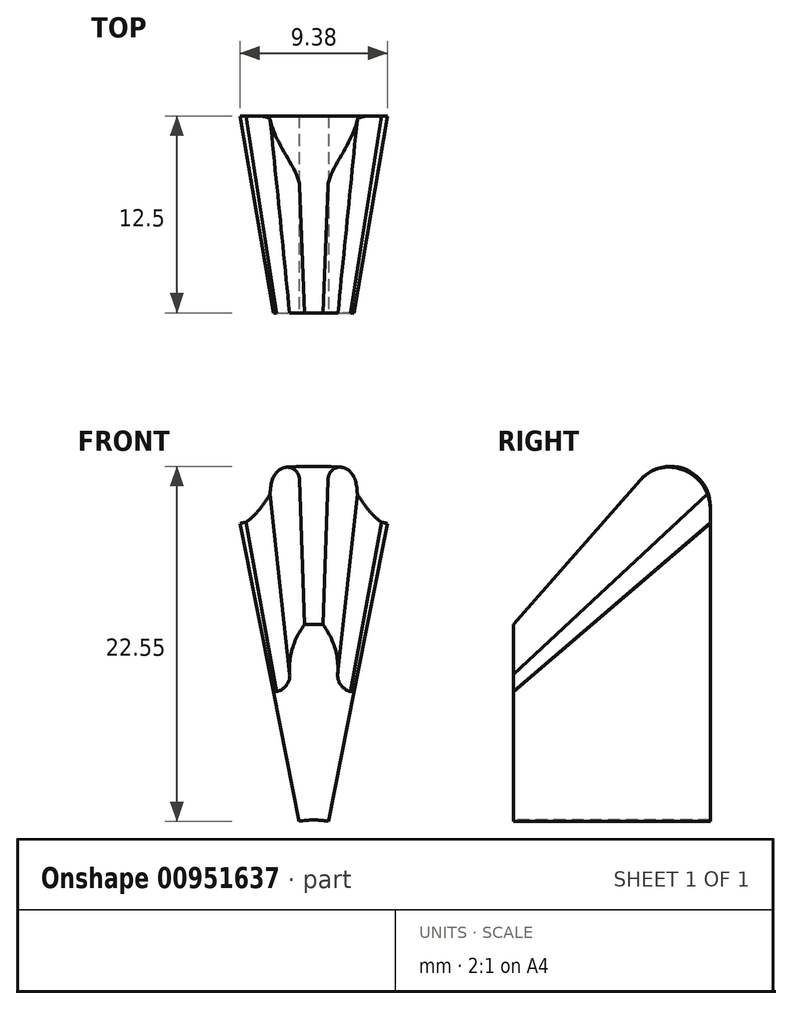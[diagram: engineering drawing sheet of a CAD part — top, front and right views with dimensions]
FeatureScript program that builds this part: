
annotation { "Feature Type Name" : "Feature", "Feature Type Description" : "" }
export const myFeature = defineFeature(function(context is Context, id is Id, definition is map)
    precondition{}
    {
        {
            var Q0;
            Q0=qCreatedBy(makeId("Front.planeOp"),FACE);
            cPlane(context, id + "F0", {"entities" : qUnion([Q0]), "cplaneType" : CPlaneType.OFFSET, "offset" : 12.7 * mm, "oppositeDirection" : true, "width" : 152.4 * mm, "height" : 152.4 * mm});
        }
        {
            assignVariable(context, id + "F1", {"name" : "GearThickness", "anyValue" : .1});
        }
        {
            var Q0;
            Q0=qCreatedBy(makeId("Front.planeOp"),FACE);
            var sketch = newSketch(context, id + "F2", { "sketchPlane" : qUnion([Q0])});
            skCircle(sketch, "E0", {"center": v(0, 0) * mm, "radius": 13 * mm});
            skSolve(sketch);
        }
        {
            var Q0;
            Q0=qSketchRegion(id+"F2",true);
            extrude(context, id + "F3", {"entities" : qUnion([Q0]), "endBound" : BoundingType.SYMMETRIC, "offsetDistance" : 25 * mm, "depth" : (getVariable(context, 'GearThickness')) * mm});
        }
        {
            var Q0;
            Q0=qCreatedBy(makeId("Front.planeOp"),FACE);
            var sketch = newSketch(context, id + "F4", { "sketchPlane" : qUnion([Q0])});
            skCircle(sketch, "E1", {"center": v(0, 0) * mm, "radius": 15 * mm, "construction": true});
            skLineSegment(sketch, "E2", {"start": v(0, 28.09) * mm, "end": v(0, 0) * mm, "construction": true});
            skLineSegment(sketch, "E3", {"start": v(0, 0) * mm, "end": v(-1.47, 14.93) * mm, "construction": true});
            skLineSegment(sketch, "E4", {"start": v(0, 0) * mm, "end": v(1.47, 14.93) * mm, "construction": true});
            skCircle(sketch, "E5", {"center": v(0, 0) * mm, "radius": 17 * mm, "construction": true});
            skArc(sketch, "E6", {"start": v(1.33, 12.93) * mm, "mid": v(0, 13) * mm, "end": v(-1.33, 12.93) * mm});
            skArc(sketch, "E7", {"start": v(0.58, 17) * mm, "mid": v(0, 17) * mm, "end": v(-0.58, 17) * mm});
            skLineSegment(sketch, "E8", {"start": v(-1.47, 14.93) * mm, "end": v(-1, 17.93) * mm, "construction": true});
            skLineSegment(sketch, "E9", {"start": v(-1.47, 14.93) * mm, "end": v(-0.58, 17) * mm, "construction": true});
            skArc(sketch, "E10", {"start": v(-0.58, 17) * mm, "mid": v(-1.45, 15.05) * mm, "end": v(-1.33, 12.93) * mm});
            skArc(sketch, "E11", {"start": v(1.33, 12.93) * mm, "mid": v(1.45, 15.05) * mm, "end": v(0.58, 17) * mm});
            skSolve(sketch);
        }
        {
            var Q0;
            Q0=qSketchRegion(id+"F4",true);
            extrude(context, id + "F5", {"entities" : qUnion([Q0]), "endBound" : BoundingType.SYMMETRIC, "depth" : (getVariable(context, 'GearThickness')) * mm});
        }
        {
            var Q0;
            Q0=qCreatedBy(makeId("Front.planeOp"),FACE);
            var sketch = newSketch(context, id + "F6", { "sketchPlane" : qUnion([Q0])});
            skArc(sketch, "E12", {"start": v(1.5, 13.86) * mm, "mid": v(1.7, 13.17) * mm, "end": v(2.32, 12.8) * mm});
            skArc(sketch, "E13", {"start": v(-2.32, 12.8) * mm, "mid": v(-1.7, 13.17) * mm, "end": v(-1.5, 13.86) * mm});
            skArc(sketch, "E14", {"start": v(2.32, 12.8) * mm, "mid": v(0, 13) * mm, "end": v(-2.32, 12.8) * mm});
            skLineSegment(sketch, "E15", {"start": v(-1.5, 13.86) * mm, "end": v(1.5, 13.86) * mm});
            skSolve(sketch);
        }
        {
            var Q0;
            Q0=qSketchRegion(id+"F6",true);
            extrude(context, id + "F7", {"entities" : qUnion([Q0]), "operationType" : NewBodyOperationType.ADD, "endBound" : BoundingType.SYMMETRIC, "offsetDistance" : 25.4 * mm, "depth" : (getVariable(context, 'GearThickness')) * mm});
        }
        {
            var Q0;
            Q0=makeQuery(id+"F3.opExtrude","CAP_FACE",FACE,{"disambiguationData":[OSD([sQuery(id+"F2.wireOp",EDGE,"E0")])],"isStart":true});
            var sketch = newSketch(context, id + "F8", { "sketchPlane" : qUnion([Q0])});
            skLineSegment(sketch, "E16", {"start": v(0, 0) * mm, "end": v(-2.32, 12.8) * mm, "construction": true});
            skLineSegment(sketch, "E17", {"start": v(0, 0) * mm, "end": v(-1.5, 13.86) * mm, "construction": true});
            skLineSegment(sketch, "E18", {"start": v(0, 0) * mm, "end": v(-0.58, 17) * mm, "construction": true});
            skLineSegment(sketch, "E19", {"start": v(0, 0) * mm, "end": v(0.58, 17) * mm, "construction": true});
            skLineSegment(sketch, "E20", {"start": v(0, 0) * mm, "end": v(1.5, 13.86) * mm, "construction": true});
            skLineSegment(sketch, "E21", {"start": v(0, 0) * mm, "end": v(2.32, 12.8) * mm, "construction": true});
            skSolve(sketch);
        }
        {
            var Q0;
            Q0=qCreatedBy(makeId("Top.planeOp"),FACE);
            var sketch = newSketch(context, id + "F9", { "sketchPlane" : qUnion([Q0])});
            skLineSegment(sketch, "E22", {"start": v(0, 0) * mm, "end": v(0, 9.45) * mm});
            skSolve(sketch);
        }
        {
            var Q0;
            Q0=sQuery(id+"F9.wireOp",VERTEX,"E22.end");
            var Q1;
            Q1=sQuery(id+"F9.wireOp",VERTEX,"E22.start");
            var Q2;
            Q2=sQuery(id+"F8.wireOp",VERTEX,"E16.end");
            cPlane(context, id + "F10", {"entities" : qUnion([Q0, Q1, Q2]), "cplaneType" : CPlaneType.THREE_POINT, "offset" : 25.4 * mm, "width" : 152.4 * mm, "height" : 152.4 * mm});
        }
        {
            var Q0;
            Q0=qCreatedBy(id+"F10.planeOp",FACE);
            var sketch = newSketch(context, id + "F11", { "sketchPlane" : qUnion([Q0])});
            skLineSegment(sketch, "E23", {"start": v(0.05, 13) * mm, "end": v(12.7, 25.65) * mm});
            skSolve(sketch);
        }
        {
            var Q0;
            Q0=sQuery(id+"F8.wireOp",VERTEX,"E20.start");
            var Q1;
            Q1=sQuery(id+"F9.wireOp",VERTEX,"E22.end");
            var Q2;
            Q2=sQuery(id+"F8.wireOp",VERTEX,"E17.end");
            cPlane(context, id + "F12", {"entities" : qUnion([Q0, Q1, Q2]), "cplaneType" : CPlaneType.THREE_POINT, "offset" : 25.4 * mm, "width" : 152.4 * mm, "height" : 152.4 * mm});
        }
        {
            var Q0;
            Q0=qCreatedBy(id+"F12.planeOp",FACE);
            var sketch = newSketch(context, id + "F13", { "sketchPlane" : qUnion([Q0])});
            skLineSegment(sketch, "E24", {"start": v(-0.05, 13.94) * mm, "end": v(-12.7, 26.6) * mm});
            skSolve(sketch);
        }
        {
            var Q0;
            Q0=sQuery(id+"F8.wireOp",VERTEX,"E18.end");
            var Q1;
            Q1=sQuery(id+"F9.wireOp",VERTEX,"E22.end");
            var Q2;
            Q2=sQuery(id+"F9.wireOp",VERTEX,"E22.start");
            cPlane(context, id + "F14", {"entities" : qUnion([Q0, Q1, Q2]), "cplaneType" : CPlaneType.THREE_POINT, "offset" : 25.4 * mm, "width" : 152.4 * mm, "height" : 152.4 * mm});
        }
        {
            var Q0;
            Q0=qCreatedBy(id+"F14.planeOp",FACE);
            var sketch = newSketch(context, id + "F15", { "sketchPlane" : qUnion([Q0])});
            skLineSegment(sketch, "E25", {"start": v(0.05, 17) * mm, "end": v(12.7, 29.65) * mm});
            skSolve(sketch);
        }
        {
            var Q0;
            Q0=sQuery(id+"F8.wireOp",VERTEX,"E20.start");
            var Q1;
            Q1=sQuery(id+"F8.wireOp",VERTEX,"E19.end");
            var Q2;
            Q2=sQuery(id+"F9.wireOp",VERTEX,"E22.end");
            cPlane(context, id + "F16", {"entities" : qUnion([Q0, Q1, Q2]), "cplaneType" : CPlaneType.THREE_POINT, "offset" : 25.4 * mm, "width" : 152.4 * mm, "height" : 152.4 * mm});
        }
        {
            var Q0;
            Q0=qCreatedBy(id+"F16.planeOp",FACE);
            var sketch = newSketch(context, id + "F17", { "sketchPlane" : qUnion([Q0])});
            skLineSegment(sketch, "E26", {"start": v(0.05, 17) * mm, "end": v(12.7, 29.65) * mm});
            skSolve(sketch);
        }
        {
            var Q0;
            Q0=sQuery(id+"F9.wireOp",VERTEX,"E22.end");
            var Q1;
            Q1=sQuery(id+"F9.wireOp",VERTEX,"E22.start");
            var Q2;
            Q2=sQuery(id+"F8.wireOp",VERTEX,"E20.end");
            cPlane(context, id + "F18", {"entities" : qUnion([Q0, Q1, Q2]), "cplaneType" : CPlaneType.THREE_POINT, "offset" : 25.4 * mm, "width" : 152.4 * mm, "height" : 152.4 * mm});
        }
        {
            var Q0;
            Q0=qCreatedBy(id+"F18.planeOp",FACE);
            var sketch = newSketch(context, id + "F19", { "sketchPlane" : qUnion([Q0])});
            skLineSegment(sketch, "E27", {"start": v(0.05, 13.94) * mm, "end": v(12.7, 26.6) * mm});
            skSolve(sketch);
        }
        {
            var Q0;
            Q0=sQuery(id+"F9.wireOp",VERTEX,"E22.end");
            var Q1;
            Q1=sQuery(id+"F8.wireOp",VERTEX,"E21.end");
            var Q2;
            Q2=sQuery(id+"F9.wireOp",VERTEX,"E22.start");
            cPlane(context, id + "F20", {"entities" : qUnion([Q0, Q1, Q2]), "cplaneType" : CPlaneType.THREE_POINT, "offset" : 25.4 * mm, "width" : 152.4 * mm, "height" : 152.4 * mm});
        }
        {
            var Q0;
            Q0=qCreatedBy(id+"F20.planeOp",FACE);
            var sketch = newSketch(context, id + "F21", { "sketchPlane" : qUnion([Q0])});
            skLineSegment(sketch, "E28", {"start": v(-0.05, 13) * mm, "end": v(-12.7, 25.65) * mm});
            skSolve(sketch);
        }
        {
            var Q0;
            Q0=qCreatedBy(id+"F0.planeOp",FACE);
            var sketch = newSketch(context, id + "F22", { "sketchPlane" : qUnion([Q0])});
            skArc(sketch, "E29", {"start": v(1.07, 31.42) * mm, "mid": v(0, 31.44) * mm, "end": v(-1.07, 31.42) * mm});
            skArc(sketch, "E30", {"start": v(-1.07, 31.42) * mm, "mid": v(-2.37, 28.66) * mm, "end": v(-2.79, 25.65) * mm});
            skArc(sketch, "E31", {"start": v(2.79, 25.65) * mm, "mid": v(2.37, 28.66) * mm, "end": v(1.07, 31.42) * mm});
            skArc(sketch, "E32", {"start": v(-4.3, 23.67) * mm, "mid": v(-3.4, 24.55) * mm, "end": v(-2.79, 25.65) * mm});
            skArc(sketch, "E33", {"start": v(2.79, 25.65) * mm, "mid": v(3.4, 24.55) * mm, "end": v(4.3, 23.67) * mm});
            skLineSegment(sketch, "E34", {"start": v(0, 0) * mm, "end": v(-4.3, 23.67) * mm, "construction": true});
            skLineSegment(sketch, "E35", {"start": v(0, 0) * mm, "end": v(-2.79, 25.65) * mm, "construction": true});
            skLineSegment(sketch, "E36", {"start": v(0, 0) * mm, "end": v(-1.07, 31.42) * mm, "construction": true});
            skLineSegment(sketch, "E37", {"start": v(0, 0) * mm, "end": v(1.07, 31.42) * mm, "construction": true});
            skLineSegment(sketch, "E38", {"start": v(0, 0) * mm, "end": v(2.79, 25.65) * mm, "construction": true});
            skLineSegment(sketch, "E39", {"start": v(0, 0) * mm, "end": v(4.3, 23.67) * mm, "construction": true});
            skLineSegment(sketch, "E40", {"start": v(0, 0) * mm, "end": v(4.7, 23.6) * mm});
            skLineSegment(sketch, "E41", {"start": v(0, 0) * mm, "end": v(-4.7, 23.6) * mm});
            skLineSegment(sketch, "E42", {"start": v(0, 0) * mm, "end": v(0, 20.32) * mm, "construction": true});
            skArc(sketch, "E43", {"start": v(-4.3, 23.67) * mm, "mid": v(-4.5, 23.63) * mm, "end": v(-4.7, 23.6) * mm});
            skArc(sketch, "E44", {"start": v(4.7, 23.6) * mm, "mid": v(4.5, 23.63) * mm, "end": v(4.3, 23.67) * mm});
            skSolve(sketch);
        }
        {
            var Q0;
            Q0=makeQuery(id+"F8.imprint","IMPRINT",FACE,{"disambiguationData":[TD([[makeQuery(id+"F8.imprint","IMPRINT",EDGE,{"derivedFrom":makeQuery(id+"F3.opExtrude","CAP_EDGE",EDGE,{"disambiguationData":[OSD([sQuery(id+"F2.wireOp",EDGE,"E0")])],"isStart":true})}),-1.0]])]});
            var sketch = newSketch(context, id + "F23", { "sketchPlane" : qUnion([Q0])});
            skLineSegment(sketch, "E45", {"start": v(0, 0) * mm, "end": v(-2.32, 12.8) * mm, "construction": true});
            skLineSegment(sketch, "E46", {"start": v(0, 0) * mm, "end": v(2.32, 12.8) * mm, "construction": true});
            skArc(sketch, "E47.0", {"start": v(-1.5, 13.86) * mm, "mid": v(-1.7, 13.17) * mm, "end": v(-2.32, 12.8) * mm});
            skArc(sketch, "E47.1", {"start": v(2.32, 12.8) * mm, "mid": v(1.7, 13.17) * mm, "end": v(1.5, 13.86) * mm});
            skArc(sketch, "E47.2", {"start": v(0.58, 17) * mm, "mid": v(1.34, 15.51) * mm, "end": v(1.5, 13.86) * mm});
            skArc(sketch, "E47.3", {"start": v(-0.58, 17) * mm, "mid": v(0, 17) * mm, "end": v(0.58, 17) * mm});
            skArc(sketch, "E47.4", {"start": v(-1.5, 13.86) * mm, "mid": v(-1.34, 15.51) * mm, "end": v(-0.58, 17) * mm});
            skLineSegment(sketch, "E48", {"start": v(0, 0) * mm, "end": v(-2.54, 12.75) * mm});
            skLineSegment(sketch, "E49", {"start": v(0, 0) * mm, "end": v(2.54, 12.75) * mm});
            skLineSegment(sketch, "E50", {"start": v(0, 0) * mm, "end": v(0, 6.32) * mm});
            skArc(sketch, "E51", {"start": v(-2.32, 12.8) * mm, "mid": v(-2.43, 12.77) * mm, "end": v(-2.54, 12.75) * mm});
            skArc(sketch, "E52", {"start": v(2.54, 12.75) * mm, "mid": v(2.43, 12.77) * mm, "end": v(2.32, 12.8) * mm});
            skSolve(sketch);
        }
        {
            var Q0;
            Q0 = qSketchRegion(id + "F22", true);
            var Q1;
            Q1 = qSketchRegion(id + "F23", true);
            var Q2;
            Q2=sQuery(id+"F23.wireOp",VERTEX,"E45.start");
            var Q3;
            Q3=sQuery(id+"F22.wireOp",VERTEX,"E34.start");
            var Q4;
            Q4=sQuery(id+"F23.wireOp",VERTEX,"E49.end");
            var Q5;
            Q5=sQuery(id+"F22.wireOp",VERTEX,"E41.end");
            var Q6;
            Q6=sQuery(id+"F23.wireOp",VERTEX,"E46.end");
            var Q7;
            Q7=sQuery(id+"F22.wireOp",VERTEX,"E32.start");
            var Q8;
            Q8=sQuery(id+"F23.wireOp",VERTEX,"E47.1.end");
            var Q9;
            Q9=sQuery(id+"F22.wireOp",VERTEX,"E30.end");
            var Q10;
            Q10=sQuery(id+"F23.wireOp",VERTEX,"E47.2.start");
            var Q11;
            Q11=sQuery(id+"F22.wireOp",VERTEX,"E29.end");
            var Q12;
            Q12=sQuery(id+"F23.wireOp",VERTEX,"E47.3.start");
            var Q13;
            Q13=sQuery(id+"F22.wireOp",VERTEX,"E29.start");
            var Q14;
            Q14=sQuery(id+"F23.wireOp",VERTEX,"E47.0.start");
            var Q15;
            Q15=sQuery(id+"F22.wireOp",VERTEX,"E31.start");
            var Q16;
            Q16=sQuery(id+"F23.wireOp",VERTEX,"E45.end");
            var Q17;
            Q17=sQuery(id+"F22.wireOp",VERTEX,"E33.end");
            var Q18;
            Q18=sQuery(id+"F23.wireOp",VERTEX,"E48.end");
            var Q19;
            Q19=sQuery(id+"F22.wireOp",VERTEX,"E40.end");
            loft(context, id + "F24", {"operationType" : NewBodyOperationType.ADD, "sheetProfilesArray" : [{ "sheetProfileEntities" : qUnion([Q0]) }, { "sheetProfileEntities" : qUnion([Q1]) }], "connections" : [{ "connectionEntities" : qUnion([Q2, Q3, Q4, Q5, Q6, Q7, Q8, Q9, Q10, Q11, Q12, Q13, Q14, Q15, Q16, Q17, Q18, Q19]), "connectionEdgeQueries" : qUnion([]), "connectionEdgeParameters" : [] }]});
        }
        {
            var Q0;
            Q0=makeQuery(id+"F24.opLoft","MID_CAP_EDGE",EDGE,{"disambiguationData":[OSD([sQuery(id+"F22.wireOp",EDGE,"E29"),sQuery(id+"F22.wireOp",EDGE,"E30"),sQuery(id+"F22.wireOp",EDGE,"E31")])],"capPos":0.0});
            fillet(context, id + "F25", {"entities" : qUnion([Q0]), "radius" : 2.54 * mm, "tangentPropagation" : true, "allowEdgeOverflow" : false});
        }
        {
            var Q0;
            Q0=makeQuery(id+"F1nLDo3oGZqNCE5_2.boolean.opBoolean","MERGE",FACE,{"derivedFrom":[makeQuery(id+"F3.opExtrude","CAP_FACE",FACE,{"disambiguationData":[OSD([sQuery(id+"F2.wireOp",EDGE,"E0")])],"isStart":false}),makeQuery(id+"F7.boolean.opBoolean","MERGE",FACE,{"derivedFrom":[makeQuery(id+"F5.opExtrude","CAP_FACE",FACE,{"disambiguationData":[OSD([sQuery(id+"F4.wireOp",EDGE,"E6"),sQuery(id+"F4.wireOp",EDGE,"E7"),sQuery(id+"F4.wireOp",EDGE,"E10"),sQuery(id+"F4.wireOp",EDGE,"E11")])],"isStart":false}),makeQuery(id+"F7.opExtrude","CAP_FACE",FACE,{"disambiguationData":[OSD([sQuery(id+"F6.wireOp",EDGE,"E12"),sQuery(id+"F6.wireOp",EDGE,"E13"),sQuery(id+"F6.wireOp",EDGE,"E14"),sQuery(id+"F6.wireOp",EDGE,"E15")])],"isStart":false})]})]});
            var sketch = newSketch(context, id + "F26", { "sketchPlane" : qUnion([Q0])});
            skCircle(sketch, "E53", {"center": v(0, 0) * mm, "radius": 4.76 * mm});
            skSolve(sketch);
        }
        {
            var Q0;
            Q0=qSketchRegion(id+"F26",true);
            extrude(context, id + "F27", {"entities" : qUnion([Q0]), "operationType" : NewBodyOperationType.REMOVE, "endBound" : BoundingType.THROUGH_ALL, "oppositeDirection" : true, "depth" : 25.4 * mm, "offsetDistance" : 25.4 * mm});
        }
        {
            var Q0;
            Q0=makeQuery(id+"F24.boolean.opBoolean","MERGE",FACE,{"derivedFrom":[makeQuery(id+"F3.opExtrude","CAP_FACE",FACE,{"disambiguationData":[OSD([sQuery(id+"F2.wireOp",EDGE,"E0")])],"isStart":false}),makeQuery(id+"F7.boolean.opBoolean","MERGE",FACE,{"derivedFrom":[makeQuery(id+"F5.opExtrude","CAP_FACE",FACE,{"disambiguationData":[OSD([sQuery(id+"F4.wireOp",EDGE,"E6"),sQuery(id+"F4.wireOp",EDGE,"E7"),sQuery(id+"F4.wireOp",EDGE,"E10"),sQuery(id+"F4.wireOp",EDGE,"E11")])],"isStart":false}),makeQuery(id+"F7.opExtrude","CAP_FACE",FACE,{"disambiguationData":[OSD([sQuery(id+"F6.wireOp",EDGE,"E12"),sQuery(id+"F6.wireOp",EDGE,"E13"),sQuery(id+"F6.wireOp",EDGE,"E14"),sQuery(id+"F6.wireOp",EDGE,"E15")])],"isStart":false})]})]});
            var sketch = newSketch(context, id + "F28", { "sketchPlane" : qUnion([Q0])});
            skCircle(sketch, "E54", {"center": v(0, 0) * mm, "radius": 38.1 * mm});
            skSolve(sketch);
        }
        {
            var Q0;
            Q0 = qSketchRegion(id + "F28", true);
            extrude(context, id + "F29", {"entities" : qUnion([Q0]), "operationType" : NewBodyOperationType.REMOVE, "oppositeDirection" : true, "depth" : 0.25 * mm, "offsetDistance" : 25.4 * mm});
        }
    });
